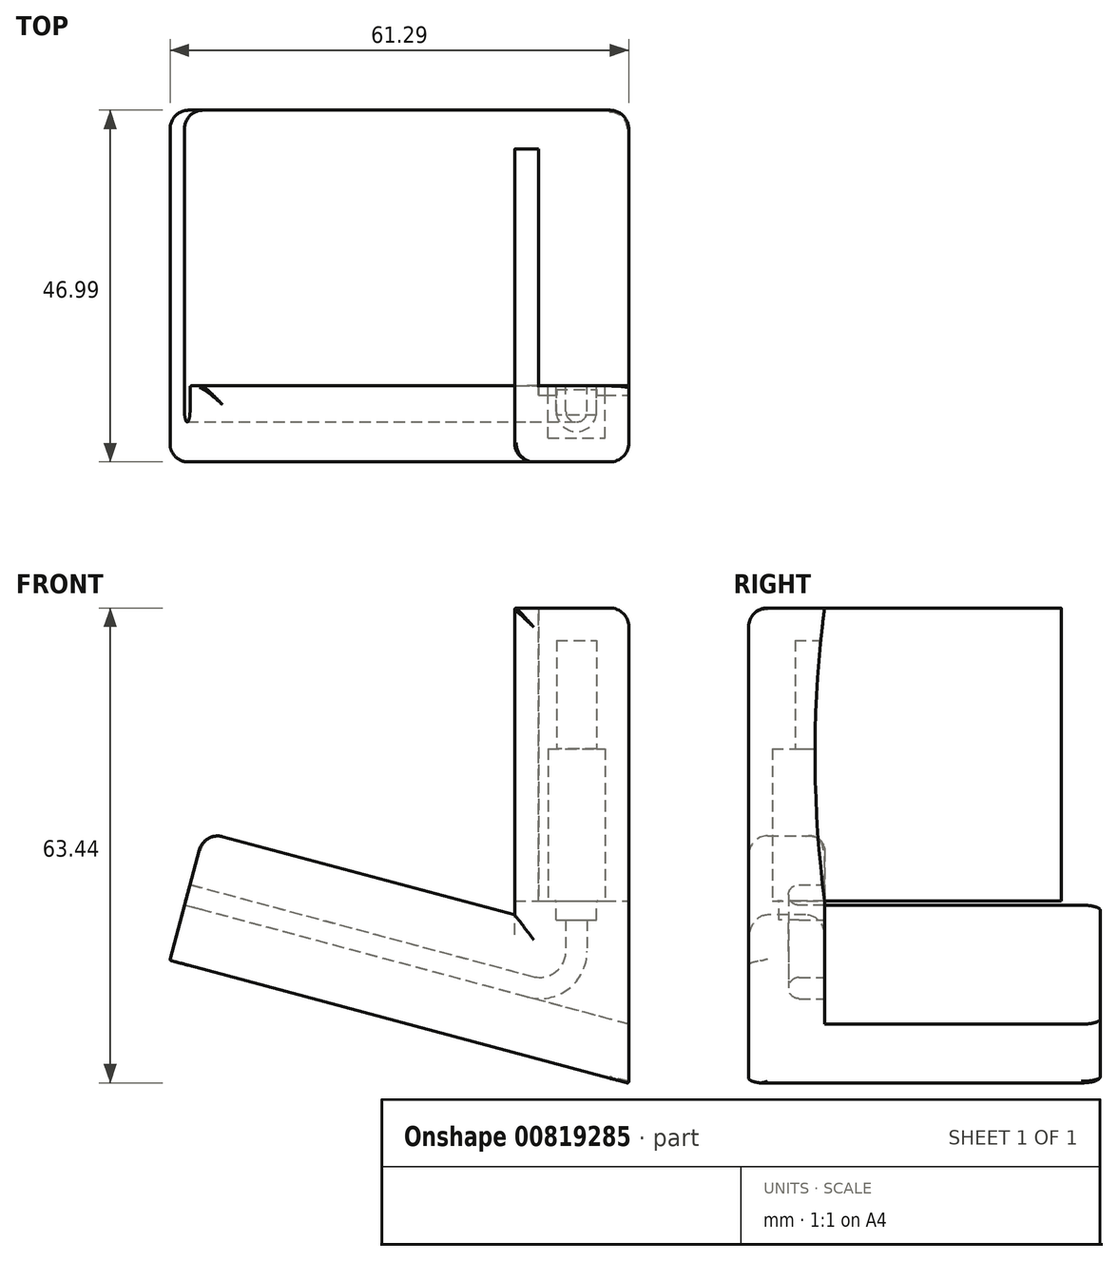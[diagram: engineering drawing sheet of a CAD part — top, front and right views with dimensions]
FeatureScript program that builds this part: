
annotation { "Feature Type Name" : "Feature", "Feature Type Description" : "" }
export const myFeature = defineFeature(function(context is Context, id is Id, definition is map)
    precondition{}
    {
        {
            var Q0;
            Q0=qCreatedBy(makeId("Right.planeOp"),FACE);
            var sketch = newSketch(context, id + "F0", { "sketchPlane" : qUnion([Q0])});
            skLineSegment(sketch, "E0.bottom", {"start": v(0, 0) * mm, "end": v(-10.16, 0) * mm});
            skLineSegment(sketch, "E0.top", {"start": v(0, 38.1) * mm, "end": v(-10.16, 38.1) * mm});
            skLineSegment(sketch, "E0.left", {"start": v(0, 0) * mm, "end": v(0, 38.1) * mm});
            skLineSegment(sketch, "E0.right", {"start": v(-10.16, 0) * mm, "end": v(-10.16, 38.1) * mm});
            skSolve(sketch);
        }
        {
            var Q0;
            Q0 = qSketchRegion(id + "F0", true);
            extrude(context, id + "F1", {"entities" : qUnion([Q0]), "oppositeDirection" : true, "depth" : 15.24 * mm, "offsetDistance" : 25.4 * mm});
        }
        {
            var Q0;
            Q0=makeQuery(id+"F1.opExtrude","SWEPT_FACE",FACE,{"disambiguationData":[OSD([sQuery(id+"F0.wireOp",EDGE,"E0.right")])]});
            var sketch = newSketch(context, id + "F2", { "sketchPlane" : qUnion([Q0])});
            skLineSegment(sketch, "E1", {"start": v(-15.24, -13.43) * mm, "end": v(-59.36, -1.6) * mm});
            skLineSegment(sketch, "E2", {"start": v(-15.24, 0) * mm, "end": v(-15.24, -13.43) * mm});
            skLineSegment(sketch, "E3", {"start": v(-59.36, -1.6) * mm, "end": v(-61.34, -8.96) * mm});
            skLineSegment(sketch, "E4", {"start": v(-61.34, -8.96) * mm, "end": v(0, -25.4) * mm});
            skLineSegment(sketch, "E5", {"start": v(0, -25.4) * mm, "end": v(0, 0) * mm});
            skLineSegment(sketch, "E6", {"start": v(0, 0) * mm, "end": v(-15.24, 0) * mm});
            skSolve(sketch);
        }
        {
            var Q0;
            Q0 = qSketchRegion(id + "F2", true);
            extrude(context, id + "F3", {"entities" : qUnion([Q0]), "operationType" : NewBodyOperationType.ADD, "oppositeDirection" : true, "depth" : 47 * mm, "offsetDistance" : 25.4 * mm});
        }
        {
            var Q0;
            Q0=makeQuery(id+"F3.boolean.opBoolean","MERGE",FACE,{"derivedFrom":[makeQuery(id+"F1.opExtrude","SWEPT_FACE",FACE,{"disambiguationData":[OSD([sQuery(id+"F0.wireOp",EDGE,"E0.right")])]}),makeQuery(id+"F3.opExtrude","CAP_FACE",FACE,{"disambiguationData":[OSD([sQuery(id+"F2.wireOp",EDGE,"E1"),sQuery(id+"F2.wireOp",EDGE,"E2"),sQuery(id+"F2.wireOp",EDGE,"E3"),sQuery(id+"F2.wireOp",EDGE,"E4"),sQuery(id+"F2.wireOp",EDGE,"E5"),sQuery(id+"F2.wireOp",EDGE,"E6")])],"isStart":true})]});
            var sketch = newSketch(context, id + "F4", { "sketchPlane" : qUnion([Q0])});
            skLineSegment(sketch, "E7", {"start": v(-59.36, -1.6) * mm, "end": v(-56.73, 8.2) * mm});
            skLineSegment(sketch, "E8", {"start": v(-56.73, 8.2) * mm, "end": v(-15.24, -2.9) * mm});
            skLineSegment(sketch, "E9", {"start": v(-59.36, -1.6) * mm, "end": v(-15.24, -13.43) * mm});
            skLineSegment(sketch, "E10", {"start": v(-15.24, -13.43) * mm, "end": v(-15.24, -2.9) * mm});
            skSolve(sketch);
        }
        {
            var Q0;
            Q0 = qSketchRegion(id + "F4", true);
            var Q1;
            Q1=makeQuery(id+"F1.opExtrude","SWEPT_FACE",FACE,{"disambiguationData":[OSD([sQuery(id+"F0.wireOp",EDGE,"E0.left")])]});
            extrude(context, id + "F5", {"entities" : qUnion([Q0]), "operationType" : NewBodyOperationType.ADD, "endBound" : BoundingType.UP_TO_SURFACE, "oppositeDirection" : true, "depth" : 25.4 * mm, "endBoundEntityFace" : qUnion([Q1]), "offsetDistance" : 25.4 * mm});
        }
        {
            var Q0;
            Q0=makeQuery(id+"F3.opExtrude","CAP_FACE",FACE,{"disambiguationData":[OSD([sQuery(id+"F2.wireOp",EDGE,"E1"),sQuery(id+"F2.wireOp",EDGE,"E2"),sQuery(id+"F2.wireOp",EDGE,"E3"),sQuery(id+"F2.wireOp",EDGE,"E4"),sQuery(id+"F2.wireOp",EDGE,"E5"),sQuery(id+"F2.wireOp",EDGE,"E6")])],"isStart":false});
            var sketch = newSketch(context, id + "F6", { "sketchPlane" : qUnion([Q0])});
            skLineSegment(sketch, "E11", {"start": v(15.24, -13.43) * mm, "end": v(0, -17.51) * mm});
            skLineSegment(sketch, "E12", {"start": v(0, -17.51) * mm, "end": v(0, 0) * mm});
            skLineSegment(sketch, "E13", {"start": v(0, 0) * mm, "end": v(15.24, 0) * mm});
            skLineSegment(sketch, "E14", {"start": v(15.24, 0) * mm, "end": v(15.24, -13.43) * mm});
            skSolve(sketch);
        }
        {
            var Q0;
            Q0 = qSketchRegion(id + "F6", true);
            var Q1;
            Q1=makeQuery(id+"F1.opExtrude","SWEPT_FACE",FACE,{"disambiguationData":[OSD([sQuery(id+"F0.wireOp",EDGE,"E0.left")])]});
            extrude(context, id + "F7", {"entities" : qUnion([Q0]), "operationType" : NewBodyOperationType.REMOVE, "endBound" : BoundingType.UP_TO_SURFACE, "oppositeDirection" : true, "depth" : 25.4 * mm, "endBoundEntityFace" : qUnion([Q1]), "offsetDistance" : 25.4 * mm});
        }
        {
            var Q0;
            Q0=makeQuery(id+"F7.boolean.opBoolean","MERGE",FACE,{"derivedFrom":[makeQuery(id+"F1.opExtrude","SWEPT_FACE",FACE,{"disambiguationData":[OSD([sQuery(id+"F0.wireOp",EDGE,"E0.left")])]}),makeQuery(id+"F5.opExtrude","CAP_FACE",FACE,{"disambiguationData":[OSD([sQuery(id+"F4.wireOp",EDGE,"E7"),sQuery(id+"F4.wireOp",EDGE,"E8"),sQuery(id+"F4.wireOp",EDGE,"E9"),sQuery(id+"F4.wireOp",EDGE,"E10")])],"isStart":false})],"fromTools":[makeQuery(id+"F7.opExtrude","CAP_FACE",FACE,{"disambiguationData":[OSD([sQuery(id+"F6.wireOp",EDGE,"E11"),sQuery(id+"F6.wireOp",EDGE,"E12"),sQuery(id+"F6.wireOp",EDGE,"E13"),sQuery(id+"F6.wireOp",EDGE,"E14")])],"isStart":false})]});
            var sketch = newSketch(context, id + "F8", { "sketchPlane" : qUnion([Q0])});
            skLineSegment(sketch, "E15.bottom", {"start": v(15.24, 38.1) * mm, "end": v(12.06, 38.1) * mm});
            skLineSegment(sketch, "E15.top", {"start": v(15.24, -1.02) * mm, "end": v(12.07, -1.02) * mm});
            skLineSegment(sketch, "E15.left", {"start": v(15.24, 38.1) * mm, "end": v(15.24, -1.02) * mm});
            skLineSegment(sketch, "E15.right", {"start": v(12.06, 38.1) * mm, "end": v(12.07, -1.02) * mm});
            skSolve(sketch);
        }
        {
            var Q0;
            Q0 = qSketchRegion(id + "F8", true);
            var Q1;
            Q1=makeQuery(id+"F3.opExtrude","CAP_FACE",FACE,{"disambiguationData":[OSD([sQuery(id+"F2.wireOp",EDGE,"E1"),sQuery(id+"F2.wireOp",EDGE,"E2"),sQuery(id+"F2.wireOp",EDGE,"E3"),sQuery(id+"F2.wireOp",EDGE,"E4"),sQuery(id+"F2.wireOp",EDGE,"E5"),sQuery(id+"F2.wireOp",EDGE,"E6")])],"isStart":false});
            extrude(context, id + "F9", {"entities" : qUnion([Q0]), "operationType" : NewBodyOperationType.ADD, "depth" : 34.16 * mm, "endBoundEntityFace" : qUnion([Q1]), "offsetDistance" : 25.4 * mm});
        }
        {
            var Q0;
            Q0=makeQuery(id+"F3.boolean.opBoolean","MERGE",FACE,{"derivedFrom":[makeQuery(id+"F1.opExtrude","CAP_FACE",FACE,{"disambiguationData":[OSD([sQuery(id+"F0.wireOp",EDGE,"E0.bottom"),sQuery(id+"F0.wireOp",EDGE,"E0.top"),sQuery(id+"F0.wireOp",EDGE,"E0.left"),sQuery(id+"F0.wireOp",EDGE,"E0.right")])],"isStart":true}),makeQuery(id+"F3.opExtrude","SWEPT_FACE",FACE,{"disambiguationData":[OSD([sQuery(id+"F2.wireOp",EDGE,"E5")])]})]});
            var sketch = newSketch(context, id + "F10", { "sketchPlane" : qUnion([Q0])});
            skArc(sketch, "E16", {"start": v(0, 38.1) * mm, "mid": v(-1.27, 18.54) * mm, "end": v(0, -1.02) * mm});
            skLineSegment(sketch, "E17", {"start": v(0, -1.02) * mm, "end": v(0, 38.1) * mm});
            skSolve(sketch);
        }
        {
            var Q0;
            Q0 = qSketchRegion(id + "F10", true);
            var Q1;
            Q1=makeQuery(id+"F9.opExtrude","SWEPT_FACE",FACE,{"disambiguationData":[OSD([sQuery(id+"F8.wireOp",EDGE,"E15.right")])]});
            extrude(context, id + "F11", {"entities" : qUnion([Q0]), "operationType" : NewBodyOperationType.REMOVE, "endBound" : BoundingType.UP_TO_SURFACE, "oppositeDirection" : true, "depth" : 25.4 * mm, "endBoundEntityFace" : qUnion([Q1]), "offsetDistance" : 25.4 * mm});
        }
        {
            var Q0;
            Q0=makeQuery(id+"F9.opExtrude","CAP_FACE",FACE,{"disambiguationData":[OSD([sQuery(id+"F8.wireOp",EDGE,"E15.bottom"),sQuery(id+"F8.wireOp",EDGE,"E15.top"),sQuery(id+"F8.wireOp",EDGE,"E15.left"),sQuery(id+"F8.wireOp",EDGE,"E15.right")])],"isStart":false});
            var sketch = newSketch(context, id + "F12", { "sketchPlane" : qUnion([Q0])});
            skLineSegment(sketch, "E18.bottom", {"start": v(10.8, 19.3) * mm, "end": v(3.18, 19.3) * mm});
            skLineSegment(sketch, "E18.top", {"start": v(10.8, -1.02) * mm, "end": v(3.18, -1.02) * mm});
            skLineSegment(sketch, "E18.left", {"start": v(10.8, 19.3) * mm, "end": v(10.8, -1.02) * mm});
            skLineSegment(sketch, "E18.right", {"start": v(3.18, 19.3) * mm, "end": v(3.18, -1.02) * mm});
            skSolve(sketch);
        }
        {
            var Q0;
            Q0 = qSketchRegion(id + "F12", true);
            extrude(context, id + "F13", {"entities" : qUnion([Q0]), "operationType" : NewBodyOperationType.REMOVE, "oppositeDirection" : true, "depth" : 41.15 * mm, "offsetDistance" : 25.4 * mm});
        }
        {
            var Q0;
            Q0=makeQuery(id+"F7.boolean.opBoolean","MERGE",FACE,{"derivedFrom":[makeQuery(id+"F1.opExtrude","SWEPT_FACE",FACE,{"disambiguationData":[OSD([sQuery(id+"F0.wireOp",EDGE,"E0.left")])]}),makeQuery(id+"F5.opExtrude","CAP_FACE",FACE,{"disambiguationData":[OSD([sQuery(id+"F4.wireOp",EDGE,"E7"),sQuery(id+"F4.wireOp",EDGE,"E8"),sQuery(id+"F4.wireOp",EDGE,"E9"),sQuery(id+"F4.wireOp",EDGE,"E10")])],"isStart":false})],"fromTools":[makeQuery(id+"F7.opExtrude","CAP_FACE",FACE,{"disambiguationData":[OSD([sQuery(id+"F6.wireOp",EDGE,"E11"),sQuery(id+"F6.wireOp",EDGE,"E12"),sQuery(id+"F6.wireOp",EDGE,"E13"),sQuery(id+"F6.wireOp",EDGE,"E14")])],"isStart":false})]});
            var sketch = newSketch(context, id + "F14", { "sketchPlane" : qUnion([Q0])});
            skLineSegment(sketch, "E19.bottom", {"start": v(9.68, -3.56) * mm, "end": v(4.3, -3.56) * mm});
            skLineSegment(sketch, "E19.top", {"start": v(9.68, 1.52) * mm, "end": v(4.3, 1.52) * mm});
            skLineSegment(sketch, "E19.left", {"start": v(9.68, -3.56) * mm, "end": v(9.68, 1.52) * mm});
            skLineSegment(sketch, "E19.right", {"start": v(4.3, -3.56) * mm, "end": v(4.3, 1.52) * mm});
            skPoint(sketch, "E19.middle", {"position": v(6.99, -1.02) * mm});
            skSolve(sketch);
        }
        {
            var Q0;
            Q0 = qSketchRegion(id + "F14", true);
            extrude(context, id + "F15", {"entities" : qUnion([Q0]), "operationType" : NewBodyOperationType.REMOVE, "oppositeDirection" : true, "depth" : 6.1 * mm, "offsetDistance" : 25.4 * mm});
        }
        {
            var Q0;
            Q0=makeQuery(id+"F15.boolean.opBoolean","COPY",EDGE,{"derivedFrom":makeQuery(id+"F15.opExtrude","CAP_EDGE",EDGE,{"disambiguationData":[OSD([sQuery(id+"F14.wireOp",EDGE,"E19.left")])],"isStart":false})});
            var Q1;
            Q1=makeQuery(id+"F15.boolean.opBoolean","COPY",EDGE,{"derivedFrom":makeQuery(id+"F15.opExtrude","CAP_EDGE",EDGE,{"disambiguationData":[OSD([sQuery(id+"F14.wireOp",EDGE,"E19.right")])],"isStart":false})});
            fillet(context, id + "F16", {"entities" : qUnion([Q0, Q1]), "radius" : 2.7 * mm, "tangentPropagation" : true, "allowEdgeOverflow" : false});
        }
        {
            var Q0;
            Q0=makeQuery(id+"F7.boolean.opBoolean","MERGE",FACE,{"derivedFrom":[makeQuery(id+"F1.opExtrude","SWEPT_FACE",FACE,{"disambiguationData":[OSD([sQuery(id+"F0.wireOp",EDGE,"E0.left")])]}),makeQuery(id+"F5.opExtrude","CAP_FACE",FACE,{"disambiguationData":[OSD([sQuery(id+"F4.wireOp",EDGE,"E7"),sQuery(id+"F4.wireOp",EDGE,"E8"),sQuery(id+"F4.wireOp",EDGE,"E9"),sQuery(id+"F4.wireOp",EDGE,"E10")])],"isStart":false})],"fromTools":[makeQuery(id+"F7.opExtrude","CAP_FACE",FACE,{"disambiguationData":[OSD([sQuery(id+"F6.wireOp",EDGE,"E11"),sQuery(id+"F6.wireOp",EDGE,"E12"),sQuery(id+"F6.wireOp",EDGE,"E13"),sQuery(id+"F6.wireOp",EDGE,"E14")])],"isStart":false})]});
            var sketch = newSketch(context, id + "F17", { "sketchPlane" : qUnion([Q0])});
            skLineSegment(sketch, "E20", {"start": v(58.63, 1.14) * mm, "end": v(12.82, -11.13) * mm});
            skLineSegment(sketch, "E21", {"start": v(6.99, -3.56) * mm, "end": v(6.99, -15.64) * mm, "construction": true});
            skLineSegment(sketch, "E22.0", {"start": v(5.56, -3.56) * mm, "end": v(5.56, -7.75) * mm});
            skLineSegment(sketch, "E23.0", {"start": v(8.4, -3.56) * mm, "end": v(8.4, -7.75) * mm});
            skLineSegment(sketch, "E24", {"start": v(13.56, -13.88) * mm, "end": v(59.36, -1.6) * mm});
            skLineSegment(sketch, "E25", {"start": v(5.56, -3.56) * mm, "end": v(8.4, -3.56) * mm});
            skLineSegment(sketch, "E26", {"start": v(59.36, -1.6) * mm, "end": v(58.63, 1.14) * mm});
            skPoint(sketch, "E27.visualSharp", {"position": v(8.4, -12.31) * mm});
            skArc(sketch, "E27.filletArc", {"start": v(8.4, -7.75) * mm, "mid": v(9.78, -10.53) * mm, "end": v(12.82, -11.13) * mm});
            skPoint(sketch, "E28.visualSharp", {"position": v(5.56, -16.02) * mm});
            skArc(sketch, "E28.filletArc", {"start": v(5.56, -7.75) * mm, "mid": v(8.05, -12.78) * mm, "end": v(13.56, -13.88) * mm});
            skSolve(sketch);
        }
        {
            var Q0;
            Q0 = qSketchRegion(id + "F17", true);
            extrude(context, id + "F18", {"entities" : qUnion([Q0]), "operationType" : NewBodyOperationType.REMOVE, "oppositeDirection" : true, "depth" : 4.83 * mm, "offsetDistance" : 25.4 * mm});
        }
        {
            var Q0;
            Q0=makeQuery(id+"F18.boolean.opBoolean","COPY",EDGE,{"derivedFrom":makeQuery(id+"F18.opExtrude","CAP_EDGE",EDGE,{"disambiguationData":[OSD([sQuery(id+"F17.wireOp",EDGE,"E23.0")])],"isStart":false})});
            var Q1;
            Q1=makeQuery(id+"F18.boolean.opBoolean","COPY",EDGE,{"derivedFrom":makeQuery(id+"F18.opExtrude","CAP_EDGE",EDGE,{"disambiguationData":[OSD([sQuery(id+"F17.wireOp",EDGE,"E22.0")])],"isStart":false})});
            fillet(context, id + "F19", {"entities" : qUnion([Q0, Q1]), "radius" : 1.42 * mm, "tangentPropagation" : true, "allowEdgeOverflow" : false});
        }
        {
            var Q0;
            Q0=makeQuery(id+"F9.opExtrude","CAP_FACE",FACE,{"disambiguationData":[OSD([sQuery(id+"F8.wireOp",EDGE,"E15.bottom"),sQuery(id+"F8.wireOp",EDGE,"E15.top"),sQuery(id+"F8.wireOp",EDGE,"E15.left"),sQuery(id+"F8.wireOp",EDGE,"E15.right")])],"isStart":false});
            var sketch = newSketch(context, id + "F20", { "sketchPlane" : qUnion([Q0])});
            skLineSegment(sketch, "E29.bottom", {"start": v(9.65, 33.78) * mm, "end": v(4.32, 33.78) * mm});
            skLineSegment(sketch, "E29.top", {"start": v(9.65, 13.46) * mm, "end": v(4.32, 13.46) * mm});
            skLineSegment(sketch, "E29.left", {"start": v(9.65, 33.78) * mm, "end": v(9.65, 13.46) * mm});
            skLineSegment(sketch, "E29.right", {"start": v(4.32, 33.78) * mm, "end": v(4.32, 13.46) * mm});
            skPoint(sketch, "E29.middle", {"position": v(6.99, 23.62) * mm});
            skLineSegment(sketch, "E30", {"start": v(6.99, 23.62) * mm, "end": v(6.99, 19.3) * mm, "construction": true});
            skSolve(sketch);
        }
        {
            var Q0;
            Q0 = qSketchRegion(id + "F20", true);
            extrude(context, id + "F21", {"entities" : qUnion([Q0]), "operationType" : NewBodyOperationType.REMOVE, "oppositeDirection" : true, "depth" : 38.1 * mm, "offsetDistance" : 25.4 * mm});
        }
        {
            var Q0;
            Q0=makeQuery(id+"F9.opExtrude","CAP_FACE",FACE,{"disambiguationData":[OSD([sQuery(id+"F8.wireOp",EDGE,"E15.bottom"),sQuery(id+"F8.wireOp",EDGE,"E15.top"),sQuery(id+"F8.wireOp",EDGE,"E15.left"),sQuery(id+"F8.wireOp",EDGE,"E15.right")])],"isStart":false});
            var sketch = newSketch(context, id + "F22", { "sketchPlane" : qUnion([Q0])});
            skLineSegment(sketch, "E31.bottom", {"start": v(12.06, 38.1) * mm, "end": v(15.24, 38.1) * mm});
            skLineSegment(sketch, "E31.top", {"start": v(12.06, -1.02) * mm, "end": v(15.24, -1.02) * mm});
            skLineSegment(sketch, "E31.left", {"start": v(12.06, 38.1) * mm, "end": v(12.06, -1.02) * mm});
            skLineSegment(sketch, "E31.right", {"start": v(15.24, 38.1) * mm, "end": v(15.24, -1.02) * mm});
            skSolve(sketch);
        }
        {
            var Q0;
            Q0 = qSketchRegion(id + "F22", true);
            extrude(context, id + "F23", {"entities" : qUnion([Q0]), "operationType" : NewBodyOperationType.REMOVE, "oppositeDirection" : true, "depth" : 2.54 * mm, "offsetDistance" : 25.4 * mm});
        }
        {
            var Q0;
            Q0=makeQuery(id+"F9.opExtrude","CAP_EDGE",EDGE,{"disambiguationData":[OSD([sQuery(id+"F8.wireOp",EDGE,"E15.top")])],"isStart":false});
            var Q1;
            Q1=makeQuery(id+"F9.opExtrude","CAP_EDGE",EDGE,{"disambiguationData":[OSD([sQuery(id+"F8.wireOp",EDGE,"E15.bottom")])],"isStart":false});
            var Q2;
            Q2=makeQuery(id+"F7.boolean.opBoolean","COPY",EDGE,{"derivedFrom":makeQuery(id+"F7.opExtrude","SWEPT_EDGE",EDGE,{"disambiguationData":[OSD([sQuery(id+"F2.wireOp",EDGE,"E5"),sQuery(id+"F6.wireOp",EDGE,"E11"),sQuery(id+"F6.wireOp",EDGE,"E12")])]})});
            var Q3;
            Q3=makeQuery(id+"F5.opExtrude","SWEPT_EDGE",EDGE,{"disambiguationData":[OSD([sQuery(id+"F4.wireOp",EDGE,"E7"),sQuery(id+"F4.wireOp",EDGE,"E8")])]});
            var Q4;
            Q4=makeQuery(id+"F3.opExtrude","CAP_EDGE",EDGE,{"disambiguationData":[OSD([sQuery(id+"F2.wireOp",EDGE,"E3")])],"isStart":false});
            var Q5;
            Q5=makeQuery(id+"F7.boolean.opBoolean","MERGE",EDGE,{"derivedFrom":[makeQuery(id+"F3.opExtrude","CAP_EDGE",EDGE,{"disambiguationData":[OSD([sQuery(id+"F2.wireOp",EDGE,"E1")])],"isStart":false})],"fromTools":[makeQuery(id+"F7.opExtrude","CAP_EDGE",EDGE,{"disambiguationData":[OSD([sQuery(id+"F6.wireOp",EDGE,"E11")])],"isStart":true})]});
            var Q6;
            Q6=makeQuery(id+"F3.opExtrude","CAP_EDGE",EDGE,{"disambiguationData":[OSD([sQuery(id+"F2.wireOp",EDGE,"E5")])],"isStart":false});
            var Q7;
            Q7=makeQuery(id+"F1.opExtrude","CAP_EDGE",EDGE,{"disambiguationData":[OSD([sQuery(id+"F0.wireOp",EDGE,"E0.top")])],"isStart":true});
            var Q8;
            Q8=makeQuery(id+"F5.opExtrude","CAP_EDGE",EDGE,{"disambiguationData":[OSD([sQuery(id+"F4.wireOp",EDGE,"E8")])],"isStart":false});
            var Q9;
            Q9=makeQuery(id+"F23.boolean.opBoolean","COPY",EDGE,{"derivedFrom":makeQuery(id+"F23.opExtrude","CAP_EDGE",EDGE,{"disambiguationData":[OSD([sQuery(id+"F22.wireOp",EDGE,"E31.bottom")])],"isStart":false})});
            var Q10;
            Q10=makeQuery(id+"F23.boolean.opBoolean","COPY",EDGE,{"derivedFrom":makeQuery(id+"F23.opExtrude","CAP_EDGE",EDGE,{"disambiguationData":[OSD([sQuery(id+"F22.wireOp",EDGE,"E31.top")])],"isStart":false})});
            var Q11;
            Q11=makeQuery(id+"F7.boolean.opBoolean","MERGE",EDGE,{"derivedFrom":[makeQuery(id+"F1.opExtrude","CAP_EDGE",EDGE,{"disambiguationData":[OSD([sQuery(id+"F0.wireOp",EDGE,"E0.left")])],"isStart":true})],"fromTools":[makeQuery(id+"F7.opExtrude","CAP_EDGE",EDGE,{"disambiguationData":[OSD([sQuery(id+"F6.wireOp",EDGE,"E12")])],"isStart":false})]});
            fillet(context, id + "F24", {"entities" : qUnion([Q0, Q1, Q2, Q3, Q4, Q5, Q6, Q7, Q8, Q9, Q10, Q11]), "radius" : 2.54 * mm, "tangentPropagation" : true, "allowEdgeOverflow" : false});
        }
        {
            var Q0;
            Q0=makeQuery(id+"F3.opExtrude","SWEPT_EDGE",EDGE,{"disambiguationData":[OSD([sQuery(id+"F2.wireOp",EDGE,"E4"),sQuery(id+"F2.wireOp",EDGE,"E5")])]});
            var Q1;
            Q1=makeQuery(id+"F15.boolean.opBoolean","INTERSECT",EDGE,{"derivedFrom":[makeQuery(id+"F13.boolean.opBoolean","COPY",FACE,{"derivedFrom":makeQuery(id+"F13.opExtrude","SWEPT_FACE",FACE,{"disambiguationData":[OSD([sQuery(id+"F12.wireOp",EDGE,"E18.top")])]})}),makeQuery(id+"F15.opExtrude","SWEPT_FACE",FACE,{"disambiguationData":[OSD([sQuery(id+"F14.wireOp",EDGE,"E19.left")])]})]});
            var Q2;
            Q2=makeQuery(id+"F18.boolean.opBoolean","COPY",EDGE,{"derivedFrom":makeQuery(id+"F18.opExtrude","SWEPT_EDGE",EDGE,{"disambiguationData":[OSD([sQuery(id+"F14.wireOp",EDGE,"E19.bottom"),sQuery(id+"F17.wireOp",EDGE,"E23.0"),sQuery(id+"F17.wireOp",EDGE,"E25")])]})});
            var Q3;
            Q3=makeQuery(id+"F18.boolean.opBoolean","MERGE",EDGE,{"derivedFrom":[makeQuery(id+"F3.opExtrude","SWEPT_EDGE",EDGE,{"disambiguationData":[OSD([sQuery(id+"F2.wireOp",EDGE,"E1"),sQuery(id+"F2.wireOp",EDGE,"E3")])]}),makeQuery(id+"F18.opExtrude","SWEPT_EDGE",EDGE,{"disambiguationData":[OSD([sQuery(id+"F17.wireOp",EDGE,"E24"),sQuery(id+"F17.wireOp",EDGE,"E26")])]})]});
            var Q4;
            Q4=makeQuery(id+"F9.boolean.opBoolean","MERGE",EDGE,{"derivedFrom":[makeQuery(id+"F1.opExtrude","CAP_EDGE",EDGE,{"disambiguationData":[OSD([sQuery(id+"F0.wireOp",EDGE,"E0.top")])],"isStart":false}),makeQuery(id+"F9.opExtrude","SWEPT_EDGE",EDGE,{"disambiguationData":[OSD([sQuery(id+"F8.wireOp",EDGE,"E15.bottom"),sQuery(id+"F8.wireOp",EDGE,"E15.left")])]})]});
            var Q5;
            Q5=makeQuery(id+"F9.opExtrude","SWEPT_EDGE",EDGE,{"disambiguationData":[OSD([sQuery(id+"F0.wireOp",EDGE,"E0.top"),sQuery(id+"F0.wireOp",EDGE,"E0.left"),sQuery(id+"F8.wireOp",EDGE,"E15.bottom"),sQuery(id+"F8.wireOp",EDGE,"E15.right")])]});
            var Q6;
            {var subQ0=sQuery(id+"F4.wireOp",EDGE,"E8");Q6=makeQuery(id+"F24.opFillet","BLEND_EDGE",EDGE,{"blendedFrom":[makeQuery(id+"F5.opExtrude","SWEPT_EDGE",EDGE,{"disambiguationData":[OSD([sQuery(id+"F4.wireOp",EDGE,"E7"),subQ0])]}),makeQuery(id+"F5.opExtrude","CAP_EDGE",EDGE,{"disambiguationData":[OSD([subQ0])],"isStart":false})],"blendedInto":[]});}
            fillet(context, id + "F25", {"entities" : qUnion([Q0, Q1, Q2, Q3, Q4, Q5, Q6]), "radius" : .2 * mm, "tangentPropagation" : true, "allowEdgeOverflow" : false});
        }
        {
            var Q0;
            Q0=makeQuery(id+"F3.boolean.opBoolean","MERGE",EDGE,{"derivedFrom":[makeQuery(id+"F1.opExtrude","CAP_EDGE",EDGE,{"disambiguationData":[OSD([sQuery(id+"F0.wireOp",EDGE,"E0.right")])],"isStart":false}),makeQuery(id+"F3.opExtrude","CAP_EDGE",EDGE,{"disambiguationData":[OSD([sQuery(id+"F2.wireOp",EDGE,"E2")])],"isStart":true})]});
            var Q1;
            Q1=makeQuery(id+"F1.opExtrude","SWEPT_EDGE",EDGE,{"disambiguationData":[OSD([sQuery(id+"F0.wireOp",EDGE,"E0.top"),sQuery(id+"F0.wireOp",EDGE,"E0.right")])]});
            var Q2;
            Q2=makeQuery(id+"F3.boolean.opBoolean","MERGE",EDGE,{"derivedFrom":[makeQuery(id+"F1.opExtrude","CAP_EDGE",EDGE,{"disambiguationData":[OSD([sQuery(id+"F0.wireOp",EDGE,"E0.right")])],"isStart":true}),makeQuery(id+"F3.opExtrude","CAP_EDGE",EDGE,{"disambiguationData":[OSD([sQuery(id+"F2.wireOp",EDGE,"E5")])],"isStart":true})]});
            var Q3;
            Q3=makeQuery(id+"F5.opExtrude","CAP_EDGE",EDGE,{"disambiguationData":[OSD([sQuery(id+"F4.wireOp",EDGE,"E8")])],"isStart":true});
            var Q4;
            Q4=makeQuery(id+"F5.boolean.opBoolean","MERGE",EDGE,{"derivedFrom":[makeQuery(id+"F3.opExtrude","CAP_EDGE",EDGE,{"disambiguationData":[OSD([sQuery(id+"F2.wireOp",EDGE,"E3")])],"isStart":true}),makeQuery(id+"F5.opExtrude","CAP_EDGE",EDGE,{"disambiguationData":[OSD([sQuery(id+"F4.wireOp",EDGE,"E7")])],"isStart":true})]});
            var Q5;
            Q5=makeQuery(id+"F24.opFillet","BLEND_EDGE",EDGE,{"blendedFrom":[makeQuery(id+"F1.opExtrude","CAP_EDGE",EDGE,{"disambiguationData":[OSD([sQuery(id+"F0.wireOp",EDGE,"E0.top")])],"isStart":true}),makeQuery(id+"F5.boolean.opBoolean","MERGE",FACE,{"derivedFrom":[makeQuery(id+"F3.boolean.opBoolean","MERGE",FACE,{"derivedFrom":[makeQuery(id+"F1.opExtrude","SWEPT_FACE",FACE,{"disambiguationData":[OSD([sQuery(id+"F0.wireOp",EDGE,"E0.right")])]}),makeQuery(id+"F3.opExtrude","CAP_FACE",FACE,{"disambiguationData":[OSD([sQuery(id+"F2.wireOp",EDGE,"E1"),sQuery(id+"F2.wireOp",EDGE,"E2"),sQuery(id+"F2.wireOp",EDGE,"E3"),sQuery(id+"F2.wireOp",EDGE,"E4"),sQuery(id+"F2.wireOp",EDGE,"E5"),sQuery(id+"F2.wireOp",EDGE,"E6")])],"isStart":true})]}),makeQuery(id+"F5.opExtrude","CAP_FACE",FACE,{"disambiguationData":[OSD([sQuery(id+"F4.wireOp",EDGE,"E7"),sQuery(id+"F4.wireOp",EDGE,"E8"),sQuery(id+"F4.wireOp",EDGE,"E9"),sQuery(id+"F4.wireOp",EDGE,"E10")])],"isStart":true})]})],"blendedInto":[makeQuery(id+"F5.boolean.opBoolean","MERGE",FACE,{"derivedFrom":[makeQuery(id+"F3.boolean.opBoolean","MERGE",FACE,{"derivedFrom":[makeQuery(id+"F1.opExtrude","SWEPT_FACE",FACE,{"disambiguationData":[OSD([sQuery(id+"F0.wireOp",EDGE,"E0.right")])]}),makeQuery(id+"F3.opExtrude","CAP_FACE",FACE,{"disambiguationData":[OSD([sQuery(id+"F2.wireOp",EDGE,"E1"),sQuery(id+"F2.wireOp",EDGE,"E2"),sQuery(id+"F2.wireOp",EDGE,"E3"),sQuery(id+"F2.wireOp",EDGE,"E4"),sQuery(id+"F2.wireOp",EDGE,"E5"),sQuery(id+"F2.wireOp",EDGE,"E6")])],"isStart":true})]}),makeQuery(id+"F5.opExtrude","CAP_FACE",FACE,{"disambiguationData":[OSD([sQuery(id+"F4.wireOp",EDGE,"E7"),sQuery(id+"F4.wireOp",EDGE,"E8"),sQuery(id+"F4.wireOp",EDGE,"E9"),sQuery(id+"F4.wireOp",EDGE,"E10")])],"isStart":true})]})]});
            fillet(context, id + "F26", {"entities" : qUnion([Q0, Q1, Q2, Q3, Q4, Q5]), "radius" : 2.54 * mm, "allowEdgeOverflow" : false});
        }
    });
